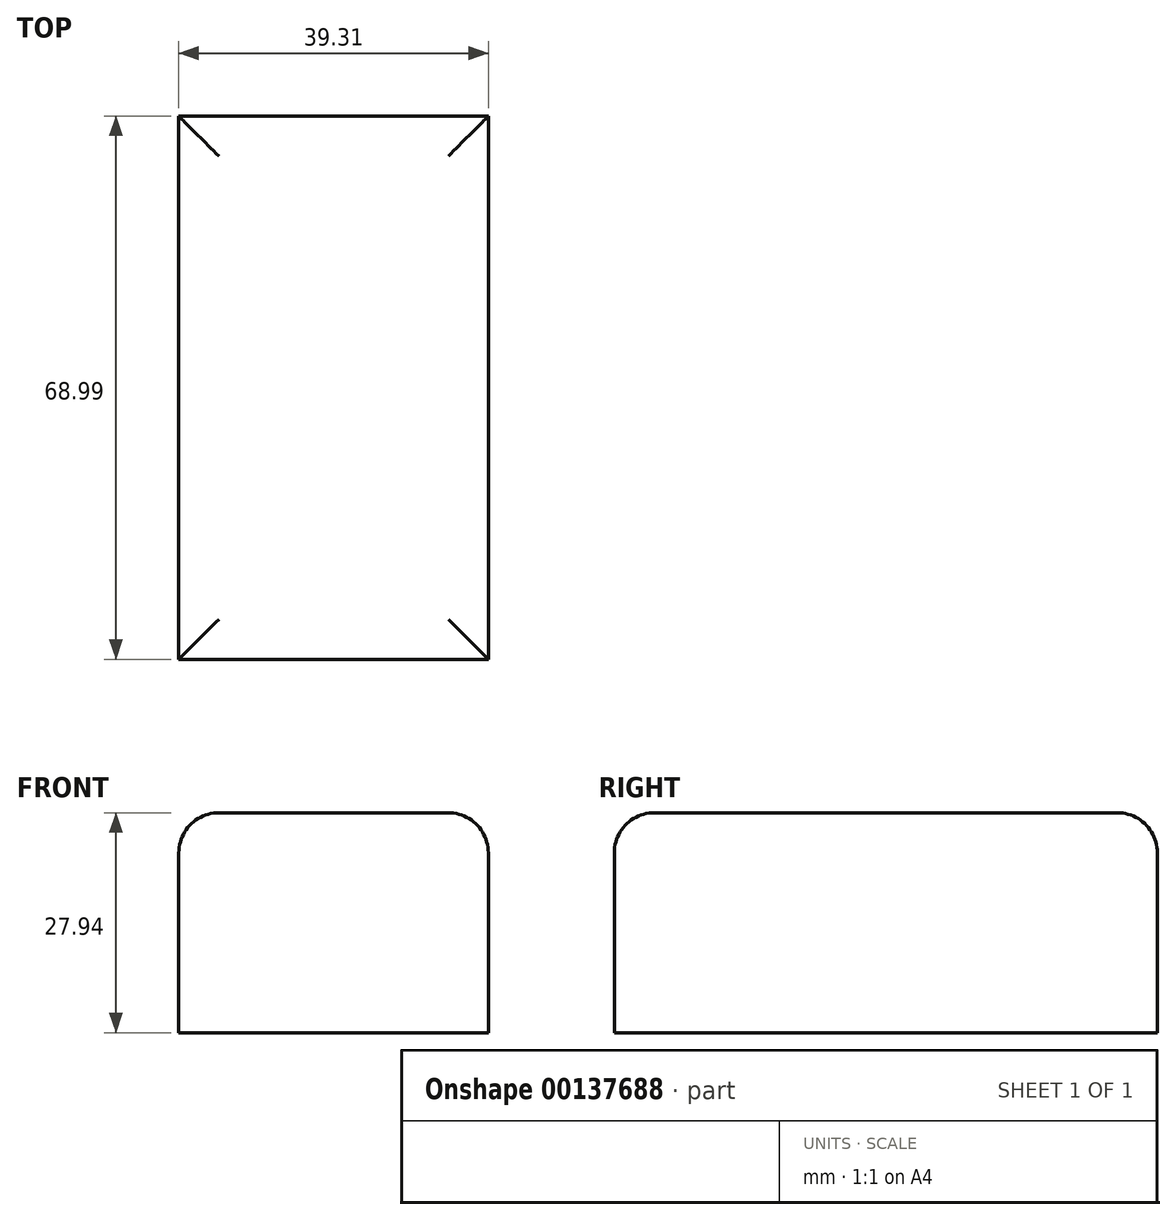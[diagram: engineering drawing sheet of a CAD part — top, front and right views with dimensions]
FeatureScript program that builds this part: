
annotation { "Feature Type Name" : "Feature", "Feature Type Description" : "" }
export const myFeature = defineFeature(function(context is Context, id is Id, definition is map)
    precondition{}
    {
        {
            var Q0;
            Q0=qCreatedBy(makeId("Top.planeOp"),FACE);
            var sketch = newSketch(context, id + "F0", { "sketchPlane" : qUnion([Q0])});
            skLineSegment(sketch, "E0.bottom", {"start": v(0, 0) * mm, "end": v(39.3, 0) * mm});
            skLineSegment(sketch, "E0.top", {"start": v(0, 69) * mm, "end": v(39.3, 69) * mm});
            skLineSegment(sketch, "E0.left", {"start": v(0, 0) * mm, "end": v(0, 69) * mm});
            skLineSegment(sketch, "E0.right", {"start": v(39.3, 0) * mm, "end": v(39.3, 69) * mm});
            skSolve(sketch);
        }
        {
            var Q0;
            Q0=makeQuery(id+"F0.imprint","IMPRINT",FACE,{"disambiguationData":[TD([[makeQuery(id+"F0.imprint","IMPRINT",EDGE,{"derivedFrom":sQuery(id+"F0.wireOp",EDGE,"E0.bottom")}),1.0]])]});
            extrude(context, id + "F1", {"entities" : qUnion([Q0]), "depth" : 27.94 * mm});
        }
        {
            var Q0;
            Q0=makeQuery(id+"F1.opExtrude","CAP_EDGE",EDGE,{"disambiguationData":[OSD([sQuery(id+"F0.wireOp",EDGE,"E0.left")])],"isStart":false});
            var Q1;
            Q1=makeQuery(id+"F1.opExtrude","CAP_EDGE",EDGE,{"disambiguationData":[OSD([sQuery(id+"F0.wireOp",EDGE,"E0.top")])],"isStart":false});
            var Q2;
            Q2=makeQuery(id+"F1.opExtrude","CAP_EDGE",EDGE,{"disambiguationData":[OSD([sQuery(id+"F0.wireOp",EDGE,"E0.right")])],"isStart":false});
            var Q3;
            Q3=makeQuery(id+"F1.opExtrude","CAP_EDGE",EDGE,{"disambiguationData":[OSD([sQuery(id+"F0.wireOp",EDGE,"E0.bottom")])],"isStart":false});
            fillet(context, id + "F2", {"entities" : qUnion([Q0, Q1, Q2, Q3]), "radius" : 5.08 * mm, "tangentPropagation" : true, "allowEdgeOverflow" : false});
        }
    });
